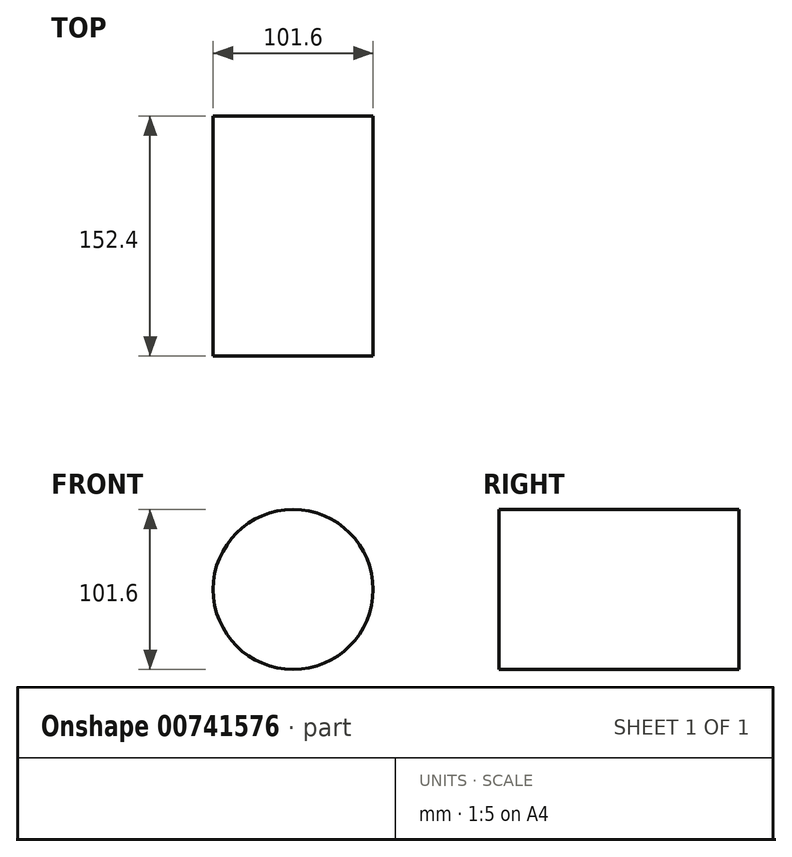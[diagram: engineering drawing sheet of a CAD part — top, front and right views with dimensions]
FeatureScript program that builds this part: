
annotation { "Feature Type Name" : "Feature", "Feature Type Description" : "" }
export const myFeature = defineFeature(function(context is Context, id is Id, definition is map)
    precondition{}
    {
        {
            var Q0;
            Q0=qCreatedBy(makeId("Front.planeOp"),FACE);
            var sketch = newSketch(context, id + "F0", { "sketchPlane" : qUnion([Q0])});
            skCircle(sketch, "E0", {"center": v(0, 0) * mm, "radius": 50.8 * mm});
            skSolve(sketch);
        }
        {
            var Q0;
            Q0=makeQuery(id+"F0.imprint","IMPRINT",FACE,{"disambiguationData":[TD([[makeQuery(id+"F0.imprint","IMPRINT",EDGE,{"derivedFrom":sQuery(id+"F0.wireOp",EDGE,"E0")}),1.0]])]});
            extrude(context, id + "F1", {"entities" : qUnion([Q0]), "depth" : 152.4 * mm, "offsetDistance" : 25.4 * mm});
        }
    });
